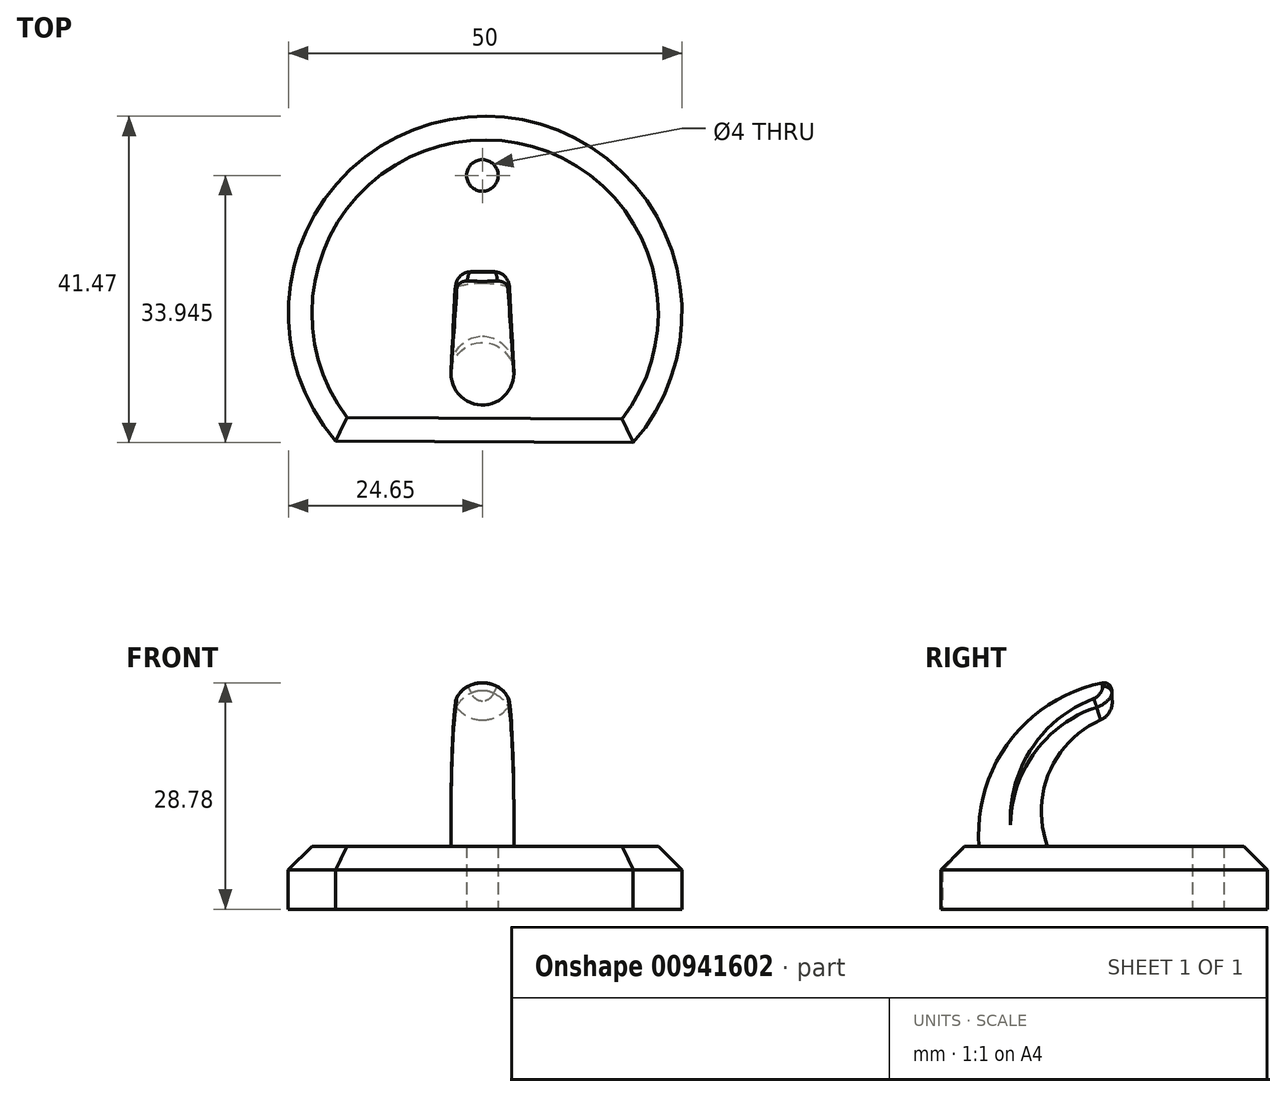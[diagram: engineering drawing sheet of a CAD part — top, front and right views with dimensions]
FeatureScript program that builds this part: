
annotation { "Feature Type Name" : "Feature", "Feature Type Description" : "" }
export const myFeature = defineFeature(function(context is Context, id is Id, definition is map)
    precondition{}
    {
        {
            var Q0;
            Q0=qCreatedBy(makeId("Top.planeOp"),FACE);
            var sketch = newSketch(context, id + "F0", { "sketchPlane" : qUnion([Q0])});
            skArc(sketch, "E0", {"start": v(19.15, -24.2) * mm, "mid": v(0.49, 17.28) * mm, "end": v(-18.65, -23.98) * mm});
            skLineSegment(sketch, "E1", {"start": v(-18.65, -23.98) * mm, "end": v(19.15, -24.2) * mm});
            skPoint(sketch, "E2", {"position": v(0, 9.75) * mm});
            skSolve(sketch);
        }
        {
            var Q0;
            Q0=qCreatedBy(makeId("Right.planeOp"),FACE);
            var sketch = newSketch(context, id + "F1", { "sketchPlane" : qUnion([Q0])});
            skLineSegment(sketch, "E3", {"start": v(-2.36, 0.23) * mm, "end": v(-17.02, 0.23) * mm});
            skArc(sketch, "E4", {"start": v(-2.55, 28.96) * mm, "mid": v(-17.32, 18.39) * mm, "end": v(-17.02, 0.23) * mm});
            skArc(sketch, "E5", {"start": v(-2.36, 24.62) * mm, "mid": v(-11.45, 12.42) * mm, "end": v(-2.36, 0.23) * mm});
            skLineSegment(sketch, "E6", {"start": v(-2.36, 24.62) * mm, "end": v(-2.55, 28.96) * mm});
            skSolve(sketch);
        }
        {
            var Q0;
            Q0=makeQuery(id+"F0.imprint","IMPRINT",FACE,{"disambiguationData":[TD([[makeQuery(id+"F0.imprint","IMPRINT",EDGE,{"derivedFrom":sQuery(id+"F0.wireOp",EDGE,"E0")}),1.0]])]});
            extrude(context, id + "F2", {"entities" : qUnion([Q0]), "depth" : 8 * mm, "offsetDistance" : 25 * mm});
        }
        {
            var Q0;
            Q0=makeQuery(id+"F2.opExtrude","CAP_FACE",FACE,{"disambiguationData":[OSD([sQuery(id+"F0.wireOp",EDGE,"E0"),sQuery(id+"F0.wireOp",EDGE,"E1")])],"isStart":false});
            chamfer(context, id + "F3", {"entities" : qUnion([Q0]), "width" : 3 * mm, "tangentPropagation" : true});
        }
        {
            var Q0;
            Q0=makeQuery(id+"F1.imprint","IMPRINT",FACE,{"disambiguationData":[TD([[makeQuery(id+"F1.imprint","IMPRINT",EDGE,{"derivedFrom":sQuery(id+"F1.wireOp",EDGE,"E3")}),-1.0]])]});
            extrude(context, id + "F4", {"entities" : qUnion([Q0]), "operationType" : NewBodyOperationType.ADD, "endBound" : BoundingType.SYMMETRIC, "depth" : 8 * mm, "offsetDistance" : 25 * mm});
        }
        {
            var Q0;
            Q0=makeQuery(id+"F4.opExtrude","CAP_EDGE",EDGE,{"disambiguationData":[OSD([sQuery(id+"F1.wireOp",EDGE,"E4")])],"isStart":false});
            var Q1;
            Q1=makeQuery(id+"F4.opExtrude","CAP_EDGE",EDGE,{"disambiguationData":[OSD([sQuery(id+"F1.wireOp",EDGE,"E4")])],"isStart":true});
            var Q2;
            Q2=makeQuery(id+"F4.opExtrude","CAP_EDGE",EDGE,{"disambiguationData":[OSD([sQuery(id+"F1.wireOp",EDGE,"E5")])],"isStart":false});
            var Q3;
            Q3=makeQuery(id+"F4.opExtrude","CAP_EDGE",EDGE,{"disambiguationData":[OSD([sQuery(id+"F1.wireOp",EDGE,"E5")])],"isStart":true});
            fillet(context, id + "F5", {"entities" : qUnion([Q0, Q1, Q2, Q3]), "radius" : 4 * mm, "tangentPropagation" : true, "allowEdgeOverflow" : false});
        }
        {
            var Q0;
            Q0=sQuery(id+"F0.wireOp",VERTEX,"E2");
            var Q1;
            Q1=makeQuery(id+"F2.opExtrude","SWEPT_BODY",BODY,{"disambiguationData":[OSD([sQuery(id+"F0.wireOp",EDGE,"E0"),sQuery(id+"F0.wireOp",EDGE,"E1")])]});
            hole(context, id + "F6", {"style" : HoleStyle.SIMPLE, "endStyle" : HoleEndStyle.THROUGH, "oppositeDirection" : true, "holeDiameter" : 4 * mm, "majorDiameter" : 5 * mm, "isTappedThrough" : true, "tappedDepth" : 12 * mm, "tapClearance" : 3, "locations" : qUnion([Q0]), "scope" : qUnion([Q1])});
        }
        {
            var Q0;
            Q0=makeQuery(id+"F5.opFillet","BLEND_EDGE",EDGE,{"blendedFrom":[makeQuery(id+"F4.opExtrude","CAP_EDGE",EDGE,{"disambiguationData":[OSD([sQuery(id+"F1.wireOp",EDGE,"E5")])],"isStart":true}),makeQuery(id+"F4.opExtrude","SWEPT_FACE",FACE,{"disambiguationData":[OSD([sQuery(id+"F1.wireOp",EDGE,"E6")])]})],"blendedInto":[makeQuery(id+"F4.opExtrude","SWEPT_FACE",FACE,{"disambiguationData":[OSD([sQuery(id+"F1.wireOp",EDGE,"E6")])]})]});
            fillet(context, id + "F7", {"entities" : qUnion([Q0]), "radius" : 2.5 * mm, "tangentPropagation" : true, "allowEdgeOverflow" : false});
        }
        {
            var Q0;
            Q0=makeQuery(id+"F5.opFillet","BLEND_EDGE",EDGE,{"blendedFrom":[makeQuery(id+"F4.opExtrude","CAP_EDGE",EDGE,{"disambiguationData":[OSD([sQuery(id+"F1.wireOp",EDGE,"E4")])],"isStart":false}),makeQuery(id+"F4.opExtrude","SWEPT_FACE",FACE,{"disambiguationData":[OSD([sQuery(id+"F1.wireOp",EDGE,"E6")])]})],"blendedInto":[makeQuery(id+"F4.opExtrude","SWEPT_FACE",FACE,{"disambiguationData":[OSD([sQuery(id+"F1.wireOp",EDGE,"E6")])]})]});
            var Q1;
            Q1=makeQuery(id+"F5.opFillet","BLEND_EDGE",EDGE,{"blendedFrom":[makeQuery(id+"F4.opExtrude","CAP_EDGE",EDGE,{"disambiguationData":[OSD([sQuery(id+"F1.wireOp",EDGE,"E4")])],"isStart":true}),makeQuery(id+"F4.opExtrude","SWEPT_FACE",FACE,{"disambiguationData":[OSD([sQuery(id+"F1.wireOp",EDGE,"E6")])]})],"blendedInto":[makeQuery(id+"F4.opExtrude","SWEPT_FACE",FACE,{"disambiguationData":[OSD([sQuery(id+"F1.wireOp",EDGE,"E6")])]})]});
            fillet(context, id + "F8", {"entities" : qUnion([Q0, Q1]), "radius" : 1 * mm, "tangentPropagation" : true, "allowEdgeOverflow" : false});
        }
    });
